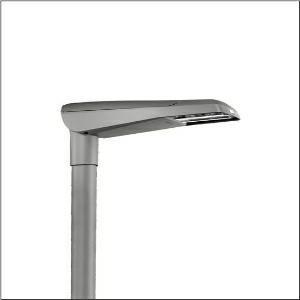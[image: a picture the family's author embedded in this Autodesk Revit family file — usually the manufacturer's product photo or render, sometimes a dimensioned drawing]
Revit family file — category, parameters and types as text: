
# Revit family: streetlight_sl_11_iq_micro___p1_0a_5xc1c41f08ce_dca2
name_source: partatom
category: Lighting Fixtures
units: mm (PartAtom-declared; Revit-internal decimal feet)

## family parameters
Cut with Voids When Loaded = No
Host = Face
Light Source = No
Part Type = Normal
Room Calculation Point = No
Round Connector Dimension = Use Diameter
Shared = No

## types (1)
- --- (1 x LED, 1660 lm, 10.8 W, 4000K)
    Apparent Load = 11 VA
    CIE Flux Codes = 29 63 93 100 100
    Color Rendering = 70
    Color Temperature = 4000K
    Default Elevation = 1800 mm
    Description = Streetlight SL 11 iQ micro, mast luminaire, primary light control with 3 zone facetted reflector, of plastic, silver coated, highly specular, primary optical cover: cover, of PMMA, transparent, light distribution: P1.0a, light emission: direct distribution, primary light characteristic: asymmetric, installation type: post-top, side-entry, lamps: LED, High Power LED, rated values: 1.660lm | 10,8W | 153,7lm/W (begin service life); end service life: 1.660lm | 11,1W; at 50% lumin. flux: 830lm | 6W | 138,3lm/W, colour temperature: 4000K, colour rendering: CRI > 70, light colour: 740, light setting 1 begin service life: 100% | 1.660lm | 10,8W | 153,7lm/W | 4.000K, light setting 1 end service life: 11,1W, further light settings possible, control: Street-Remote, optimised constant luminous flux control (CLO 2.0), Desk-Remote (wireless, voltage-free reading and setting of iQ features in the workshop via application-optimized NFC function/RFID function), Light-Fading, Smart-Wire, Night-Set, Lumen-Switch, Temp-Guard, Auto-Match, with cable H07RN-F 5x 1.5mm², mains connection: 230..240V, AC, 50/60Hz, connection cable pre-assembled, cable length: 5,5m, luminaire housing, of diecast aluminium, powder-coated, Siteco® metallic grey (DB 702S), please order mast flange separately, inclination adjustable without tools: 0°, 5°, 10°, 15° (post-top) | 0°, -5°, -10°, -15° (side-entry), sealing non-destructively replaceable, multi-level sealing system, length: 600mm, width: 174mm, height: 116mm, mast flange for spigot size: 42mm (side-entry): 5XC10008XM4, 60/48mm (side-entry/post-top): 5XC10108XM2, 76/60mm (side-entry/post-top): 5XC10108XM1, equipment: standard, protection rating (complete): IP66, insulation class (complete): insulation class II (safety insulation), certification: CE, ENEC, ENEC+, VDE, impact resistance: IK10, permissible operating ambient temperature for outdoor applications: -25..+50°C, standard-compliant lighting for roads and squares, Environmental Product Declaration (EPD) tested and certified by an independent institute, packaging unit: 1 piece

Light Distribution: P1.0a
    Height = 116 mm
    Lamp = 1 x LED
    Lamp Light Flux = 1660 lm
    Lamp Power = 10.8 W
    Lamp count = 1
    Length = 600 mm
    Luminous efficacy = 154 lm/W
    Manufacturer = Siteco
    ModVariant = No
    Model = 5XC1C41F08CE
    Number of Poles = 1
    OnlyDefault = Yes
    Power Factor = 1
    Product Name = Streetlight SL 11 iQ micro | P1.0a
    Product group = mast luminaire | pylon top
    ProductGroupID = 6100
    Protection Class = Protection class II
    Protection Degree = IP 66
    RLX_Detail_Level = 1
    RLX_Emergency_Light_Flux = 0 lm
    RLX_Emergency_Type = 0
    RLX_Emergency_Type_DB = No
    RlxData = <blob elided: 26585 chars, md5=d3556186>
    Socket = socket
    Standby Power = 0 W
    System Light Flux = 1660 lm
    System Power = 11 W
    Type Comments = factory setting: luminous flux: 100 % | dim-lin: 254 | 194 mA
    Type Image = l_1006566.jpg
    URL = http://relux.com
    VarID = @adj_018213
    Voltage = 0 V
    Weight = 0.00 kg
    Width = 174 mm

## geometry (parser evidence)
native form markers: Blend x4, Sweep x11
no freeform markers — native parametric forms only
